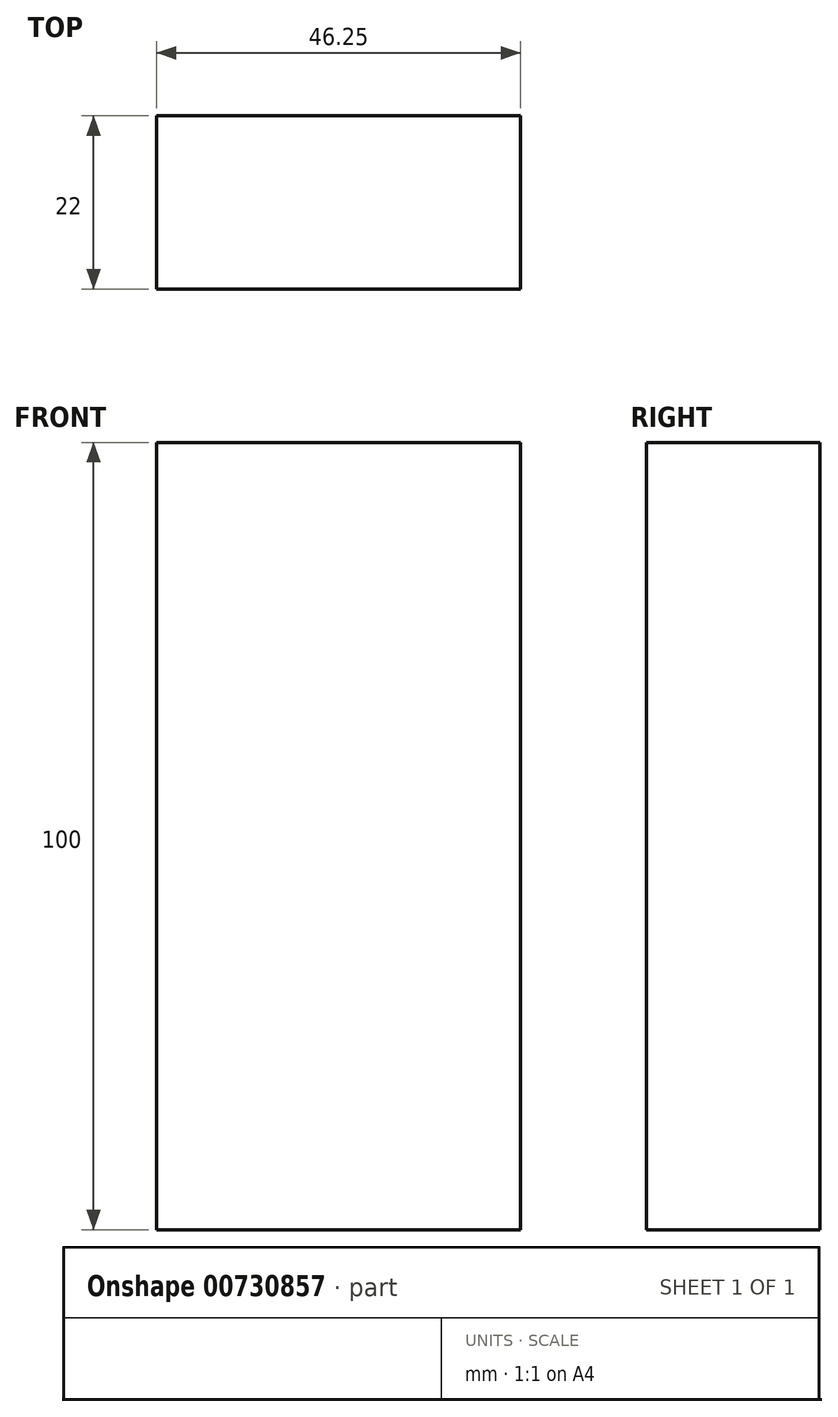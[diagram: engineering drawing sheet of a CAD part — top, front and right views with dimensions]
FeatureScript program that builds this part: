
annotation { "Feature Type Name" : "Feature", "Feature Type Description" : "" }
export const myFeature = defineFeature(function(context is Context, id is Id, definition is map)
    precondition{}
    {
        {
            var Q0;
            Q0=qCreatedBy(makeId("Top.planeOp"),FACE);
            var sketch = newSketch(context, id + "F0", { "sketchPlane" : qUnion([Q0])});
            skLineSegment(sketch, "E0.bottom", {"start": v(0, 0) * mm, "end": v(46.25, 0) * mm});
            skLineSegment(sketch, "E0.top", {"start": v(0, -22) * mm, "end": v(46.25, -22) * mm});
            skLineSegment(sketch, "E0.left", {"start": v(0, 0) * mm, "end": v(0, -22) * mm});
            skLineSegment(sketch, "E0.right", {"start": v(46.25, 0) * mm, "end": v(46.25, -22) * mm});
            skLineSegment(sketch, "E1.bottom", {"start": v(16.36, 0) * mm, "end": v(24.96, 0) * mm});
            skLineSegment(sketch, "E1.top", {"start": v(16.36, 11.14) * mm, "end": v(24.96, 11.14) * mm});
            skLineSegment(sketch, "E1.left", {"start": v(16.36, 0) * mm, "end": v(16.36, 11.14) * mm});
            skLineSegment(sketch, "E1.right", {"start": v(24.96, 0) * mm, "end": v(24.96, 11.14) * mm});
            skSolve(sketch);
        }
        {
            var Q0;
            Q0 = qSketchRegion(id + "F0", true);
            var sketch = newSketch(context, id + "F1", { "sketchPlane" : qUnion([Q0])});
            skSolve(sketch);
        }
        {
            var Q0;
            Q0=makeQuery(id+"F1.imprint","IMPRINT",FACE,{"disambiguationData":[TD([[makeQuery(id+"F1.imprint","IMPRINT",EDGE,{"derivedFrom":makeQuery(id+"F0.imprint","IMPRINT",EDGE,{"derivedFrom":sQuery(id+"F0.wireOp",EDGE,"E0.top")})}),1.0]])]});
            extrude(context, id + "F2", {"entities" : qUnion([Q0]), "depth" : 100 * mm, "offsetDistance" : 25.4 * mm});
        }
    });
